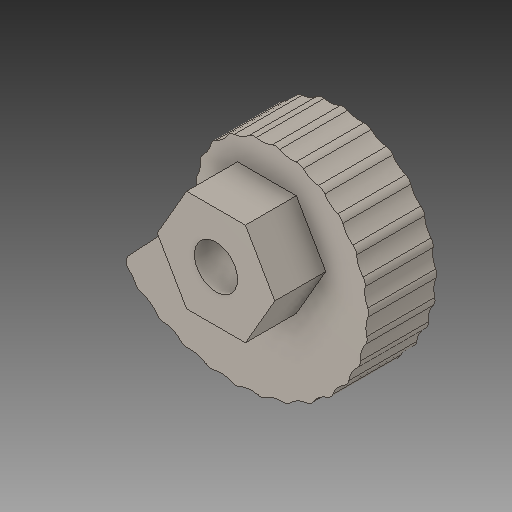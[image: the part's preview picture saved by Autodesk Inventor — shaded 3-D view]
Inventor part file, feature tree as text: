
AUTODESK INVENTOR PART (.ipt)
format: ipt  version: 2017 (Build 210142000, 142)  size: 185,344 bytes
history: native  units: in
note: dims shown in document units (in); Inventor stores cm internally (conversion verified against a paired STEP export)
features: fillet x1
ambient origin geometry x8: Origin, YZ Plane, XZ Plane, XY Plane, X Axis, Y Axis, Z Axis, Center Point
bodies: Solid1 (feature_tree)
feature tree (1):
  fillet  "Fillet1"  [1 undecoded]
note: 1 required parameter value undecoded (feature->parameter linkage not recoverable at this tier; creation-order binding heuristic only, values carry confidence <= 0.55)
